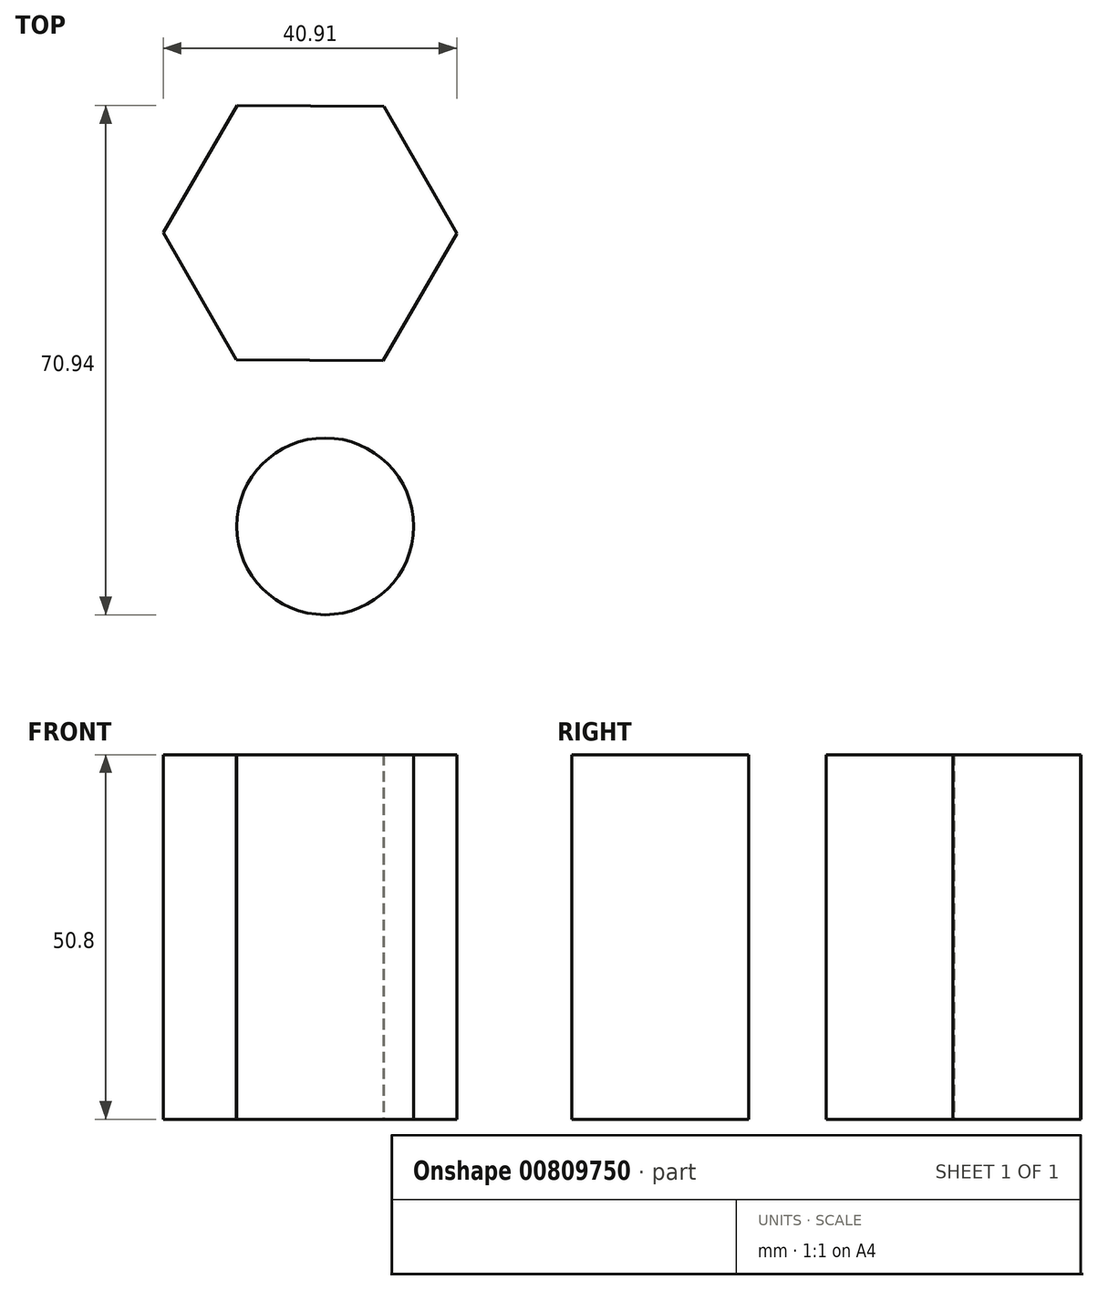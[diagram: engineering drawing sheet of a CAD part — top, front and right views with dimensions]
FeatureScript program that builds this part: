
annotation { "Feature Type Name" : "Feature", "Feature Type Description" : "" }
export const myFeature = defineFeature(function(context is Context, id is Id, definition is map)
    precondition{}
    {
        {
            var Q0;
            Q0=qCreatedBy(makeId("Top.planeOp"),FACE);
            var sketch = newSketch(context, id + "F0", { "sketchPlane" : qUnion([Q0])});
            skCircle(sketch, "E0", {"center": v(0, 0) * mm, "radius": 12.32 * mm});
            skSolve(sketch);
        }
        {
            var Q0;
            Q0 = qSketchRegion(id + "F0", true);
            extrude(context, id + "F1", {"entities" : qUnion([Q0]), "depth" : 50.8 * mm, "offsetDistance" : 25.4 * mm});
        }
        {
            var Q0;
            Q0=qCreatedBy(makeId("Top.planeOp"),FACE);
            var sketch = newSketch(context, id + "F2", { "sketchPlane" : qUnion([Q0])});
            skCircle(sketch, "E1.cCircle", {"center": v(-2.11, 40.86) * mm, "radius": 17.72 * mm, "construction": true});
            skLineSegment(sketch, "E1.0", {"start": v(-12.4, 23.19) * mm, "end": v(-22.57, 40.94) * mm});
            skLineSegment(sketch, "E1.1", {"start": v(-22.57, 40.94) * mm, "end": v(-12.27, 58.62) * mm});
            skLineSegment(sketch, "E1.2", {"start": v(-12.27, 58.62) * mm, "end": v(8.18, 58.54) * mm});
            skLineSegment(sketch, "E1.3", {"start": v(8.18, 58.54) * mm, "end": v(18.34, 40.79) * mm});
            skLineSegment(sketch, "E1.4", {"start": v(18.34, 40.79) * mm, "end": v(8.05, 23.1) * mm});
            skLineSegment(sketch, "E1.5", {"start": v(8.05, 23.1) * mm, "end": v(-12.4, 23.19) * mm});
            skPoint(sketch, "E1.0.midPoint", {"position": v(-17.49, 32.06) * mm});
            skSolve(sketch);
        }
        {
            var Q0;
            Q0 = qSketchRegion(id + "F2", true);
            extrude(context, id + "F3", {"entities" : qUnion([Q0]), "depth" : 50.8 * mm, "offsetDistance" : 25.4 * mm});
        }
    });
